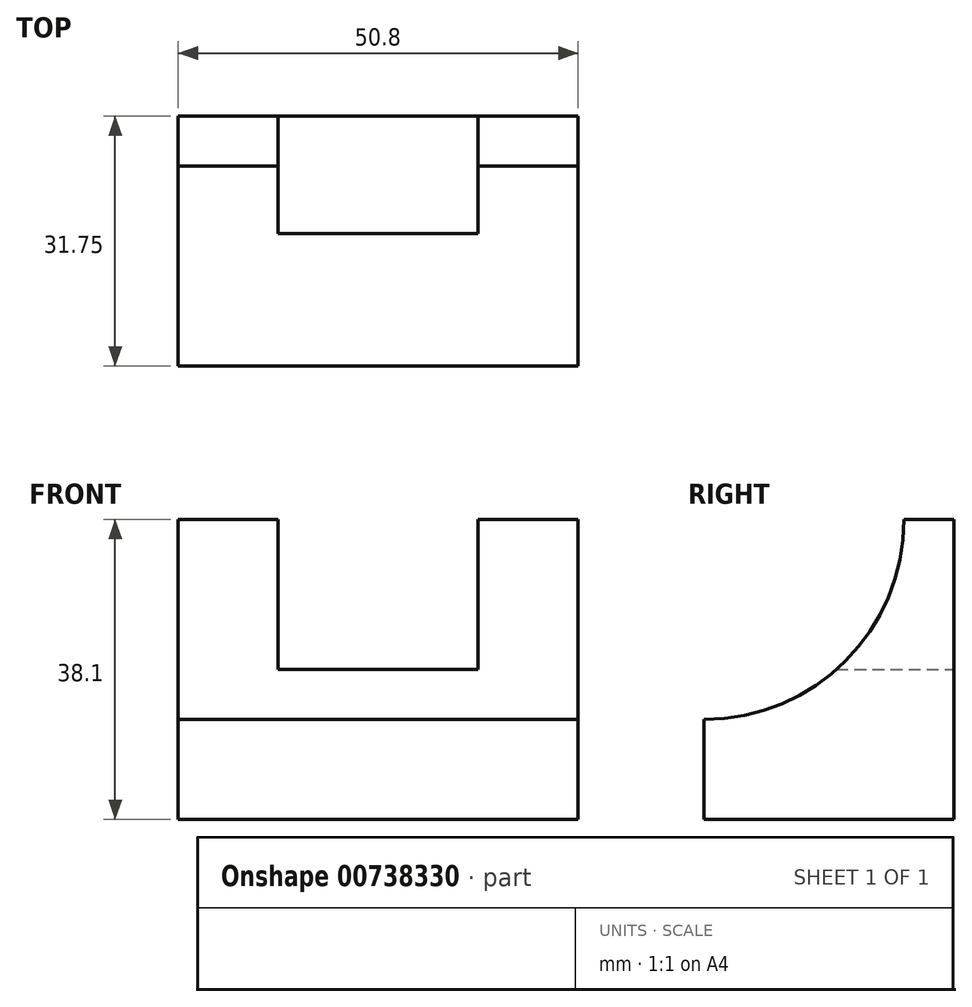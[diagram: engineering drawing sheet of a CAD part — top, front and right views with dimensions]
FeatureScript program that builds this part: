
annotation { "Feature Type Name" : "Feature", "Feature Type Description" : "" }
export const myFeature = defineFeature(function(context is Context, id is Id, definition is map)
    precondition{}
    {
        {
            var Q0;
            Q0=qCreatedBy(makeId("Front.planeOp"),FACE);
            var sketch = newSketch(context, id + "F0", { "sketchPlane" : qUnion([Q0])});
            skLineSegment(sketch, "E0", {"start": v(-26.87, 0) * mm, "end": v(-26.87, 38.1) * mm});
            skLineSegment(sketch, "E1", {"start": v(-26.87, 38.1) * mm, "end": v(23.93, 38.1) * mm});
            skLineSegment(sketch, "E2", {"start": v(23.93, 38.1) * mm, "end": v(23.93, 0) * mm});
            skLineSegment(sketch, "E3", {"start": v(23.93, 0) * mm, "end": v(-26.87, 0) * mm});
            skSolve(sketch);
        }
        {
            var Q0;
            Q0=makeQuery(id+"F0.imprint","IMPRINT",FACE,{"disambiguationData":[TD([[makeQuery(id+"F0.imprint","IMPRINT",EDGE,{"derivedFrom":sQuery(id+"F0.wireOp",EDGE,"E0")}),-1.0]])]});
            extrude(context, id + "F1", {"entities" : qUnion([Q0]), "depth" : 31.75 * mm, "offsetDistance" : 25.4 * mm});
        }
        {
            var Q0;
            Q0=makeQuery(id+"F1.opExtrude","CAP_FACE",FACE,{"disambiguationData":[OSD([sQuery(id+"F0.wireOp",EDGE,"E0"),sQuery(id+"F0.wireOp",EDGE,"E1"),sQuery(id+"F0.wireOp",EDGE,"E2"),sQuery(id+"F0.wireOp",EDGE,"E3")])],"isStart":true});
            var sketch = newSketch(context, id + "F2", { "sketchPlane" : qUnion([Q0])});
            skLineSegment(sketch, "E4", {"start": v(-23.93, 38.1) * mm, "end": v(-11.23, 38.1) * mm});
            skLineSegment(sketch, "E5", {"start": v(-11.23, 38.1) * mm, "end": v(-11.23, 19.05) * mm});
            skLineSegment(sketch, "E6", {"start": v(-11.23, 19.05) * mm, "end": v(14.17, 19.05) * mm});
            skLineSegment(sketch, "E7", {"start": v(14.17, 19.05) * mm, "end": v(14.17, 38.1) * mm});
            skLineSegment(sketch, "E8", {"start": v(14.17, 38.1) * mm, "end": v(26.87, 38.1) * mm});
            skSolve(sketch);
        }
        {
            var Q0;
            {var subQ0=sQuery(id+"F2.wireOp",EDGE,"E5");Q0=makeQuery(id+"F2.imprint","IMPRINT",FACE,{"disambiguationData":[TD([[makeQuery(id+"F2.imprint","IMPRINT",EDGE,{"derivedFrom":subQ0}),1.0]])]});}
            extrude(context, id + "F3", {"entities" : qUnion([Q0]), "operationType" : NewBodyOperationType.REMOVE, "endBound" : BoundingType.THROUGH_ALL, "oppositeDirection" : true, "depth" : 25.4 * mm, "offsetDistance" : 25.4 * mm});
        }
        {
            var Q0;
            Q0=makeQuery(id+"F1.opExtrude","SWEPT_FACE",FACE,{"disambiguationData":[OSD([sQuery(id+"F0.wireOp",EDGE,"E2")])]});
            var sketch = newSketch(context, id + "F4", { "sketchPlane" : qUnion([Q0])});
            skCircle(sketch, "E9", {"center": v(-31.75, 38.1) * mm, "radius": 25.4 * mm});
            skSolve(sketch);
        }
        {
            var Q0;
            {var subQ0=sQuery(id+"F4.wireOp",EDGE,"E9");var subQ1=sQuery(id+"F0.wireOp",EDGE,"E2");var subQ4=makeQuery(id+"F1.opExtrude","CAP_EDGE",EDGE,{"disambiguationData":[OSD([subQ1])],"isStart":false});var subQ5=makeQuery(id+"F4.imprint","INTERSECT",VERTEX,{"derivedFrom":[subQ4,subQ0]});Q0=makeQuery(id+"F4.imprint","IMPRINT",FACE,{"disambiguationData":[TD([[makeQuery(id+"F4.imprint","IMPRINT",EDGE,{"disambiguationData":[TD([[subQ5,-1.0]])],"derivedFrom":subQ0}),1.0]])]});}
            extrude(context, id + "F5", {"entities" : qUnion([Q0]), "operationType" : NewBodyOperationType.REMOVE, "endBound" : BoundingType.THROUGH_ALL, "oppositeDirection" : true, "depth" : 25.4 * mm, "offsetDistance" : 25.4 * mm});
        }
    });
